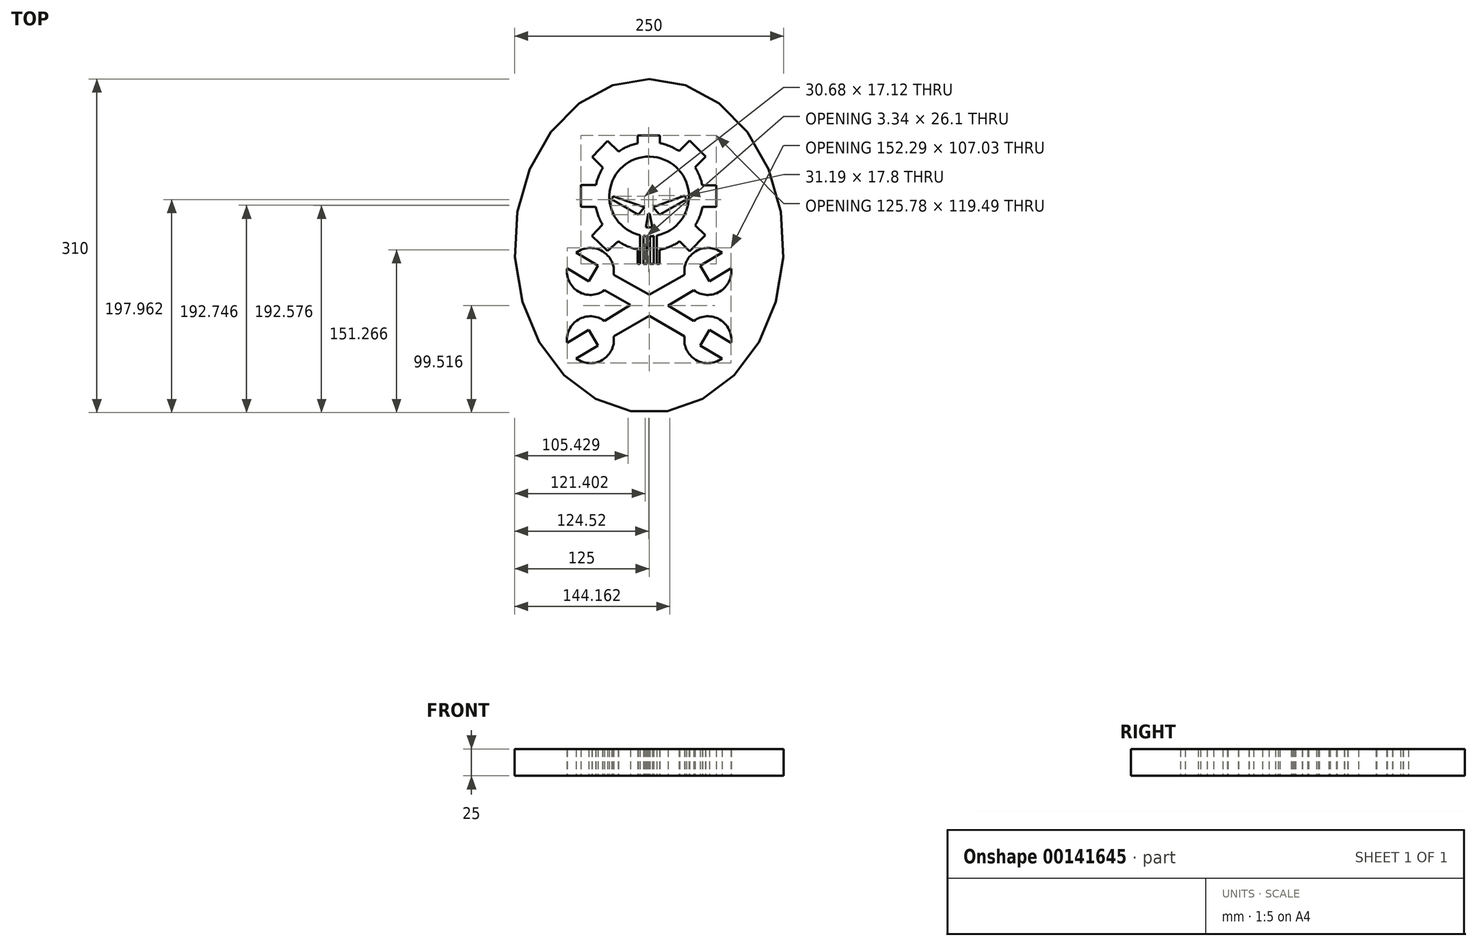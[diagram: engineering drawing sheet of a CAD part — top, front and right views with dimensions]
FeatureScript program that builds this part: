
annotation { "Feature Type Name" : "Feature", "Feature Type Description" : "" }
export const myFeature = defineFeature(function(context is Context, id is Id, definition is map)
    precondition{}
    {
        {
            var Q0;
            Q0=qCreatedBy(makeId("Top.planeOp"),FACE);
            var sketch = newSketch(context, id + "F0", { "sketchPlane" : qUnion([Q0])});
            skArc(sketch, "E0", {"start": v(-5.27, 9.32) * mm, "mid": v(-3.6, 9.12) * mm, "end": v(-1.93, 8.99) * mm});
            skLineSegment(sketch, "E1", {"start": v(-10.52, 95.33) * mm, "end": v(-10.52, 102.7) * mm});
            skLineSegment(sketch, "E2", {"start": v(-10.52, 102.7) * mm, "end": v(9.85, 102.7) * mm});
            skLineSegment(sketch, "E3", {"start": v(9.85, 102.7) * mm, "end": v(9.85, 95.46) * mm});
            skLineSegment(sketch, "E4", {"start": v(27.72, 88.14) * mm, "end": v(37.55, 97.84) * mm});
            skLineSegment(sketch, "E5", {"start": v(37.55, 97.84) * mm, "end": v(52.42, 82.79) * mm});
            skLineSegment(sketch, "E6", {"start": v(52.42, 82.79) * mm, "end": v(42.58, 73.07) * mm});
            skLineSegment(sketch, "E7", {"start": v(49.4, 56.35) * mm, "end": v(62.41, 56.35) * mm});
            skLineSegment(sketch, "E8", {"start": v(62.41, 56.35) * mm, "end": v(62.41, 36.3) * mm});
            skLineSegment(sketch, "E9", {"start": v(62.41, 36.3) * mm, "end": v(49.57, 36.3) * mm});
            skLineSegment(sketch, "E10", {"start": v(42.75, 19.06) * mm, "end": v(52.16, 10) * mm});
            skLineSegment(sketch, "E11", {"start": v(52.16, 10) * mm, "end": v(37.72, -5) * mm});
            skLineSegment(sketch, "E12", {"start": v(37.72, -5) * mm, "end": v(28.29, 4.1) * mm});
            skLineSegment(sketch, "E13", {"start": v(-28.6, 4.3) * mm, "end": v(-38.44, -4.65) * mm});
            skLineSegment(sketch, "E14", {"start": v(-38.44, -4.65) * mm, "end": v(-53.1, 9.4) * mm});
            skLineSegment(sketch, "E15", {"start": v(-53.1, 9.4) * mm, "end": v(-43.19, 19.73) * mm});
            skLineSegment(sketch, "E16", {"start": v(-49.4, 56.51) * mm, "end": v(-63.37, 56.51) * mm});
            skLineSegment(sketch, "E17", {"start": v(-63.37, 56.51) * mm, "end": v(-63.37, 36.28) * mm});
            skLineSegment(sketch, "E18", {"start": v(-63.37, 36.28) * mm, "end": v(-49.58, 36.28) * mm});
            skLineSegment(sketch, "E19", {"start": v(-42.89, 72.62) * mm, "end": v(-52.96, 82.5) * mm});
            skLineSegment(sketch, "E20", {"start": v(-52.96, 82.5) * mm, "end": v(-38.7, 97.6) * mm});
            skLineSegment(sketch, "E21", {"start": v(-38.7, 97.6) * mm, "end": v(-28.3, 87.77) * mm});
            skLineSegment(sketch, "E22", {"start": v(3.57, 35.88) * mm, "end": v(9.75, 28.85) * mm});
            skLineSegment(sketch, "E23", {"start": v(9.75, 28.85) * mm, "end": v(34.76, 43.09) * mm});
            skLineSegment(sketch, "E24", {"start": v(34.76, 43.09) * mm, "end": v(33.06, 46.65) * mm});
            skLineSegment(sketch, "E25", {"start": v(33.06, 46.65) * mm, "end": v(3.57, 35.88) * mm});
            skLineSegment(sketch, "E26", {"start": v(-34.91, 43.26) * mm, "end": v(-33.39, 46.14) * mm});
            skLineSegment(sketch, "E27", {"start": v(-33.39, 46.14) * mm, "end": v(-4.23, 35.97) * mm});
            skLineSegment(sketch, "E28", {"start": v(-4.23, 35.97) * mm, "end": v(-10.08, 29.02) * mm});
            skLineSegment(sketch, "E29", {"start": v(-10.08, 29.02) * mm, "end": v(-34.91, 43.26) * mm});
            skLineSegment(sketch, "E30", {"start": v(-2.94, 17.2) * mm, "end": v(2.91, 17.2) * mm});
            skLineSegment(sketch, "E31", {"start": v(2.91, 17.2) * mm, "end": v(0.5, 30.02) * mm});
            skLineSegment(sketch, "E32", {"start": v(0.5, 30.02) * mm, "end": v(-0.66, 30.02) * mm});
            skLineSegment(sketch, "E33", {"start": v(-0.66, 30.02) * mm, "end": v(-2.94, 17.2) * mm});
            skLineSegment(sketch, "E34", {"start": v(-5.27, 9.32) * mm, "end": v(-5.27, -16.78) * mm});
            skLineSegment(sketch, "E35", {"start": v(-5.27, -16.78) * mm, "end": v(-1.93, -16.78) * mm});
            skLineSegment(sketch, "E36", {"start": v(-1.93, -16.78) * mm, "end": v(-1.93, 8.99) * mm});
            skLineSegment(sketch, "E37", {"start": v(0.83, 8.95) * mm, "end": v(0.83, -16.78) * mm});
            skLineSegment(sketch, "E38", {"start": v(0.83, -16.78) * mm, "end": v(4.2, -16.78) * mm});
            skLineSegment(sketch, "E39", {"start": v(4.2, -16.78) * mm, "end": v(4.2, 9.18) * mm});
            skLineSegment(sketch, "E40", {"start": v(7.22, 9.65) * mm, "end": v(7.22, -16.78) * mm});
            skLineSegment(sketch, "E41", {"start": v(7.22, -16.78) * mm, "end": v(9.78, -16.78) * mm});
            skLineSegment(sketch, "E42", {"start": v(9.78, -16.78) * mm, "end": v(9.78, -3.62) * mm});
            skLineSegment(sketch, "E43", {"start": v(-8.33, 9.89) * mm, "end": v(-8.33, -16.78) * mm});
            skLineSegment(sketch, "E44", {"start": v(-8.33, -16.78) * mm, "end": v(-10.72, -16.78) * mm});
            skLineSegment(sketch, "E45", {"start": v(-10.72, -16.78) * mm, "end": v(-10.72, -3.43) * mm});
            skArc(sketch, "E46.trimOffspring", {"start": v(9.78, -3.62) * mm, "mid": v(19.42, -0.7) * mm, "end": v(28.29, 4.1) * mm});
            skArc(sketch, "E47.trimOffspring", {"start": v(0.83, 8.95) * mm, "mid": v(2.52, 9.03) * mm, "end": v(4.2, 9.18) * mm});
            skArc(sketch, "E48.trimOffspring", {"start": v(7.22, 9.65) * mm, "mid": v(0.57, 82.9) * mm, "end": v(-8.33, 9.89) * mm});
            skArc(sketch, "E49.trimOffspring", {"start": v(42.75, 19.06) * mm, "mid": v(46.96, 27.36) * mm, "end": v(49.57, 36.3) * mm});
            skArc(sketch, "E50.trimOffspring", {"start": v(49.4, 56.35) * mm, "mid": v(46.75, 65.02) * mm, "end": v(42.58, 73.07) * mm});
            skArc(sketch, "E51.trimOffspring", {"start": v(-28.6, 4.3) * mm, "mid": v(-20.04, -0.44) * mm, "end": v(-10.72, -3.43) * mm});
            skArc(sketch, "E52.trimOffspring", {"start": v(-49.58, 36.28) * mm, "mid": v(-47.12, 27.72) * mm, "end": v(-43.19, 19.73) * mm});
            skArc(sketch, "E53.trimOffspring", {"start": v(-42.89, 72.62) * mm, "mid": v(-46.84, 64.85) * mm, "end": v(-49.4, 56.51) * mm});
            skArc(sketch, "E54.trimOffspring", {"start": v(-10.52, 95.33) * mm, "mid": v(-19.77, 92.4) * mm, "end": v(-28.3, 87.77) * mm});
            skArc(sketch, "E55.trimOffspring", {"start": v(27.72, 88.14) * mm, "mid": v(19.14, 92.66) * mm, "end": v(9.85, 95.46) * mm});
            skLineSegment(sketch, "E56", {"start": v(32.96, -26.8) * mm, "end": v(0, -45.24) * mm});
            skLineSegment(sketch, "E57", {"start": v(0, -45.24) * mm, "end": v(-32.96, -26.8) * mm});
            skLineSegment(sketch, "E58", {"start": v(-41.56, -41.25) * mm, "end": v(-17.4, -54.99) * mm});
            skLineSegment(sketch, "E59", {"start": v(-17.4, -54.99) * mm, "end": v(-41.56, -69.72) * mm});
            skLineSegment(sketch, "E60", {"start": v(-32.96, -84.16) * mm, "end": v(0, -64.92) * mm});
            skLineSegment(sketch, "E61", {"start": v(0, -64.92) * mm, "end": v(32.96, -84.16) * mm});
            skLineSegment(sketch, "E62", {"start": v(41.56, -69.72) * mm, "end": v(17.57, -55.48) * mm});
            skLineSegment(sketch, "E63", {"start": v(17.57, -55.48) * mm, "end": v(41.56, -41.25) * mm});
            skArc(sketch, "E64", {"start": v(41.56, -41.25) * mm, "mid": v(65.66, -42.5) * mm, "end": v(76.15, -20.77) * mm});
            skLineSegment(sketch, "E65", {"start": v(67.67, -6.33) * mm, "end": v(47.3, -18.34) * mm});
            skLineSegment(sketch, "E66", {"start": v(47.3, -18.34) * mm, "end": v(55.92, -32.8) * mm});
            skLineSegment(sketch, "E67", {"start": v(55.92, -32.8) * mm, "end": v(76.15, -20.77) * mm});
            skArc(sketch, "E68.trimOffspring", {"start": v(67.67, -6.33) * mm, "mid": v(43.47, -4.96) * mm, "end": v(32.96, -26.8) * mm});
            skLineSegment(sketch, "E69", {"start": v(0, 71.2) * mm, "end": v(0, -56.27) * mm, "construction": true});
            skLineSegment(sketch, "E70.MirrorCS", {"start": v(-55.92, -32.8) * mm, "end": v(-76.15, -20.77) * mm});
            skLineSegment(sketch, "E71.MirrorCS", {"start": v(-67.67, -6.33) * mm, "end": v(-47.3, -18.34) * mm});
            skLineSegment(sketch, "E72.MirrorCS", {"start": v(-47.3, -18.34) * mm, "end": v(-55.92, -32.8) * mm});
            skArc(sketch, "E73.MirrorCS", {"start": v(-67.67, -6.33) * mm, "mid": v(-43.47, -4.96) * mm, "end": v(-32.96, -26.8) * mm});
            skArc(sketch, "E74.MirrorCS", {"start": v(-41.56, -41.25) * mm, "mid": v(-65.66, -42.5) * mm, "end": v(-76.15, -20.77) * mm});
            skLineSegment(sketch, "E75", {"start": v(17.57, -55.48) * mm, "end": v(78.65, -55.48) * mm, "construction": true});
            skArc(sketch, "E76.MirrorCS", {"start": v(41.56, -69.72) * mm, "mid": v(65.66, -68.47) * mm, "end": v(76.15, -90.2) * mm});
            skLineSegment(sketch, "E77.MirrorCS", {"start": v(55.92, -78.16) * mm, "end": v(76.15, -90.2) * mm});
            skLineSegment(sketch, "E78.MirrorCS", {"start": v(67.67, -104.64) * mm, "end": v(47.3, -92.63) * mm});
            skLineSegment(sketch, "E79.MirrorCS", {"start": v(47.3, -92.63) * mm, "end": v(55.92, -78.16) * mm});
            skArc(sketch, "E80.MirrorCS", {"start": v(67.67, -104.64) * mm, "mid": v(43.47, -106) * mm, "end": v(32.96, -84.16) * mm});
            skArc(sketch, "E81.MirrorCS", {"start": v(-67.67, -104.64) * mm, "mid": v(-43.47, -106) * mm, "end": v(-32.96, -84.16) * mm});
            skLineSegment(sketch, "E82.MirrorCS", {"start": v(-67.67, -104.64) * mm, "end": v(-47.3, -92.63) * mm});
            skLineSegment(sketch, "E83.MirrorCS", {"start": v(-55.92, -78.16) * mm, "end": v(-76.15, -90.2) * mm});
            skLineSegment(sketch, "E84.MirrorCS", {"start": v(-47.3, -92.63) * mm, "end": v(-55.92, -78.16) * mm});
            skArc(sketch, "E85.MirrorCS", {"start": v(-41.56, -69.72) * mm, "mid": v(-65.66, -68.47) * mm, "end": v(-76.15, -90.2) * mm});
            skSolve(sketch);
        }
        {
            var Q0;
            Q0=makeQuery(id+"F0.imprint","IMPRINT",FACE,{"disambiguationData":[TD([[makeQuery(id+"F0.imprint","IMPRINT",EDGE,{"derivedFrom":sQuery(id+"F0.wireOp",EDGE,"E1")}),-1.0]])]});
            var Q1;
            Q1=makeQuery(id+"F0.imprint","IMPRINT",FACE,{"disambiguationData":[TD([[makeQuery(id+"F0.imprint","IMPRINT",EDGE,{"derivedFrom":sQuery(id+"F0.wireOp",EDGE,"E26")}),-1.0]])]});
            var Q2;
            Q2=makeQuery(id+"F0.imprint","IMPRINT",FACE,{"disambiguationData":[TD([[makeQuery(id+"F0.imprint","IMPRINT",EDGE,{"derivedFrom":sQuery(id+"F0.wireOp",EDGE,"E22")}),1.0]])]});
            var Q3;
            Q3=makeQuery(id+"F0.imprint","IMPRINT",FACE,{"disambiguationData":[TD([[makeQuery(id+"F0.imprint","IMPRINT",EDGE,{"derivedFrom":sQuery(id+"F0.wireOp",EDGE,"E30")}),1.0]])]});
            var Q4;
            Q4=makeQuery(id+"F0.imprint","IMPRINT",FACE,{"disambiguationData":[TD([[makeQuery(id+"F0.imprint","IMPRINT",EDGE,{"derivedFrom":sQuery(id+"F0.wireOp",EDGE,"E37")}),1.0]])]});
            var Q5;
            Q5=makeQuery(id+"F0.imprint","IMPRINT",FACE,{"disambiguationData":[TD([[makeQuery(id+"F0.imprint","IMPRINT",EDGE,{"derivedFrom":sQuery(id+"F0.wireOp",EDGE,"E0")}),-1.0]])]});
            var Q6;
            Q6=makeQuery(id+"F0.imprint","IMPRINT",FACE,{"disambiguationData":[TD([[makeQuery(id+"F0.imprint","IMPRINT",EDGE,{"derivedFrom":sQuery(id+"F0.wireOp",EDGE,"E56")}),1.0]])]});
            extrude(context, id + "F1", {"entities" : qUnion([Q0, Q1, Q2, Q3, Q4, Q5, Q6]), "depth" : 25 * mm});
        }
        {
            var Q0;
            Q0=qCreatedBy(makeId("Top.planeOp"),FACE);
            var sketch = newSketch(context, id + "F2", { "sketchPlane" : qUnion([Q0])});
            skEllipse(sketch, "E86", {"center": v(0, 0) * mm, "majorRadius": 155 * mm, "minorRadius": 125 * mm, "majorAxis": v(0, 1)});
            skSolve(sketch);
        }
        {
            var Q0;
            Q0=makeQuery(id+"F2.imprint","IMPRINT",FACE,{"disambiguationData":[TD([[makeQuery(id+"F2.imprint","IMPRINT",EDGE,{"derivedFrom":sQuery(id+"F2.wireOp",EDGE,"E86")}),1.0]])]});
            extrude(context, id + "F3", {"entities" : qUnion([Q0]), "depth" : 25 * mm});
        }
        {
            var Q0;
            Q0=makeQuery(id+"F1.opExtrude","SWEPT_BODY",BODY,{"disambiguationData":[OSD([sQuery(id+"F0.wireOp",EDGE,"E0"),sQuery(id+"F0.wireOp",EDGE,"E34"),sQuery(id+"F0.wireOp",EDGE,"E35"),sQuery(id+"F0.wireOp",EDGE,"E36")])]});
            var Q1;
            Q1=makeQuery(id+"F1.opExtrude","SWEPT_BODY",BODY,{"disambiguationData":[OSD([sQuery(id+"F0.wireOp",EDGE,"E1"),sQuery(id+"F0.wireOp",EDGE,"E2"),sQuery(id+"F0.wireOp",EDGE,"E3"),sQuery(id+"F0.wireOp",EDGE,"E4"),sQuery(id+"F0.wireOp",EDGE,"E5"),sQuery(id+"F0.wireOp",EDGE,"E6"),sQuery(id+"F0.wireOp",EDGE,"E7"),sQuery(id+"F0.wireOp",EDGE,"E8"),sQuery(id+"F0.wireOp",EDGE,"E9"),sQuery(id+"F0.wireOp",EDGE,"E10"),sQuery(id+"F0.wireOp",EDGE,"E11"),sQuery(id+"F0.wireOp",EDGE,"E12"),sQuery(id+"F0.wireOp",EDGE,"E13"),sQuery(id+"F0.wireOp",EDGE,"E14"),sQuery(id+"F0.wireOp",EDGE,"E15"),sQuery(id+"F0.wireOp",EDGE,"E16"),sQuery(id+"F0.wireOp",EDGE,"E17"),sQuery(id+"F0.wireOp",EDGE,"E18"),sQuery(id+"F0.wireOp",EDGE,"E19"),sQuery(id+"F0.wireOp",EDGE,"E20"),sQuery(id+"F0.wireOp",EDGE,"E21"),sQuery(id+"F0.wireOp",EDGE,"E40"),sQuery(id+"F0.wireOp",EDGE,"E41"),sQuery(id+"F0.wireOp",EDGE,"E42"),sQuery(id+"F0.wireOp",EDGE,"E43"),sQuery(id+"F0.wireOp",EDGE,"E44"),sQuery(id+"F0.wireOp",EDGE,"E45"),sQuery(id+"F0.wireOp",EDGE,"E46.trimOffspring"),sQuery(id+"F0.wireOp",EDGE,"E48.trimOffspring"),sQuery(id+"F0.wireOp",EDGE,"E49.trimOffspring"),sQuery(id+"F0.wireOp",EDGE,"E50.trimOffspring"),sQuery(id+"F0.wireOp",EDGE,"E51.trimOffspring"),sQuery(id+"F0.wireOp",EDGE,"E52.trimOffspring"),sQuery(id+"F0.wireOp",EDGE,"E53.trimOffspring"),sQuery(id+"F0.wireOp",EDGE,"E54.trimOffspring"),sQuery(id+"F0.wireOp",EDGE,"E55.trimOffspring")])]});
            var Q2;
            Q2=makeQuery(id+"F1.opExtrude","SWEPT_BODY",BODY,{"disambiguationData":[OSD([sQuery(id+"F0.wireOp",EDGE,"E22"),sQuery(id+"F0.wireOp",EDGE,"E23"),sQuery(id+"F0.wireOp",EDGE,"E24"),sQuery(id+"F0.wireOp",EDGE,"E25")])]});
            var Q3;
            Q3=makeQuery(id+"F1.opExtrude","SWEPT_BODY",BODY,{"disambiguationData":[OSD([sQuery(id+"F0.wireOp",EDGE,"E26"),sQuery(id+"F0.wireOp",EDGE,"E27"),sQuery(id+"F0.wireOp",EDGE,"E28"),sQuery(id+"F0.wireOp",EDGE,"E29")])]});
            var Q4;
            Q4=makeQuery(id+"F1.opExtrude","SWEPT_BODY",BODY,{"disambiguationData":[OSD([sQuery(id+"F0.wireOp",EDGE,"E30"),sQuery(id+"F0.wireOp",EDGE,"E31"),sQuery(id+"F0.wireOp",EDGE,"E32"),sQuery(id+"F0.wireOp",EDGE,"E33")])]});
            var Q5;
            Q5=makeQuery(id+"F1.opExtrude","SWEPT_BODY",BODY,{"disambiguationData":[OSD([sQuery(id+"F0.wireOp",EDGE,"E37"),sQuery(id+"F0.wireOp",EDGE,"E38"),sQuery(id+"F0.wireOp",EDGE,"E39"),sQuery(id+"F0.wireOp",EDGE,"E47.trimOffspring")])]});
            var Q6;
            Q6=makeQuery(id+"F1.opExtrude","SWEPT_BODY",BODY,{"disambiguationData":[OSD([sQuery(id+"F0.wireOp",EDGE,"E56"),sQuery(id+"F0.wireOp",EDGE,"E57"),sQuery(id+"F0.wireOp",EDGE,"E58"),sQuery(id+"F0.wireOp",EDGE,"E59"),sQuery(id+"F0.wireOp",EDGE,"E60"),sQuery(id+"F0.wireOp",EDGE,"E61"),sQuery(id+"F0.wireOp",EDGE,"E62"),sQuery(id+"F0.wireOp",EDGE,"E63"),sQuery(id+"F0.wireOp",EDGE,"E64"),sQuery(id+"F0.wireOp",EDGE,"E65"),sQuery(id+"F0.wireOp",EDGE,"E66"),sQuery(id+"F0.wireOp",EDGE,"E67"),sQuery(id+"F0.wireOp",EDGE,"E68.trimOffspring"),sQuery(id+"F0.wireOp",EDGE,"E74.MirrorCS"),sQuery(id+"F0.wireOp",EDGE,"E70.MirrorCS"),sQuery(id+"F0.wireOp",EDGE,"E71.MirrorCS"),sQuery(id+"F0.wireOp",EDGE,"E72.MirrorCS"),sQuery(id+"F0.wireOp",EDGE,"E73.MirrorCS"),sQuery(id+"F0.wireOp",EDGE,"E76.MirrorCS"),sQuery(id+"F0.wireOp",EDGE,"E77.MirrorCS"),sQuery(id+"F0.wireOp",EDGE,"E78.MirrorCS"),sQuery(id+"F0.wireOp",EDGE,"E79.MirrorCS"),sQuery(id+"F0.wireOp",EDGE,"E80.MirrorCS"),sQuery(id+"F0.wireOp",EDGE,"E81.MirrorCS"),sQuery(id+"F0.wireOp",EDGE,"E82.MirrorCS"),sQuery(id+"F0.wireOp",EDGE,"E83.MirrorCS"),sQuery(id+"F0.wireOp",EDGE,"E84.MirrorCS"),sQuery(id+"F0.wireOp",EDGE,"E85.MirrorCS")])]});
            var Q7;
            Q7=makeQuery(id+"F3.opExtrude","SWEPT_BODY",BODY,{"disambiguationData":[OSD([sQuery(id+"F2.wireOp",EDGE,"E86")])]});
            booleanBodies(context, id + "F4", {"operationType" : BooleanOperationType.SUBTRACTION, "tools" : qUnion([Q0, Q1, Q2, Q3, Q4, Q5, Q6]), "targets" : qUnion([Q7])});
        }
    });
